# Revit family: Grid_Drain-DXV-Oak_Hill-D35155460_Series
name_source: partatom
category: Plumbing Fixtures
units: mm (PartAtom-declared; Revit-internal decimal feet)

## family parameters
Always vertical = No
Cut with Voids When Loaded = No
OmniClass Number = 23.70.50.21.24
OmniClass Title = Waste Water Drains
Part Type = Normal
Room Calculation Point = No
Round Connector Dimension = Use Diameter
Shared = Yes
Work Plane-Based = Yes

## types (4) — shared parameters
Assembly Code = D2030
CW Connection = No
Default Elevation = 0"
Description = Grid Drain
HW Connection = No
Manufacturer = DXV
Price = Prices may vary. Please consult Manufacturer Representative for most up-to-date price list.
URL = https://www.dxv.com
Vent Connection = No
Waste Connection = Yes
Waste Connection Diameter = 1 1/4"
Waste Connection Radius = 5/8"
Width = 2 3/8"

## per-type parameters (varying)
| type | Finish | Material |
| D35155460.100 | Brass-DXV-100-Polished Chrome | Brass-DXV-100-Polished Chrome |
| D35155460.144 | Brass-DXV-144-Brushed Nickel | Brass-DXV-144-Brushed Nickel |
| D35155460.150 | Brass-DXV-150-Platinum Nickel | Brass-DXV-150-Platinum Nickel |
| D35155460.427 | Brass-DXV-427-Satin Brass | Brass-DXV-427-Satin Brass |

note: column(s) folded — value = type name in every type: Model

## geometry (parser evidence)
native form markers: Sweep x2
no freeform markers — native parametric forms only
